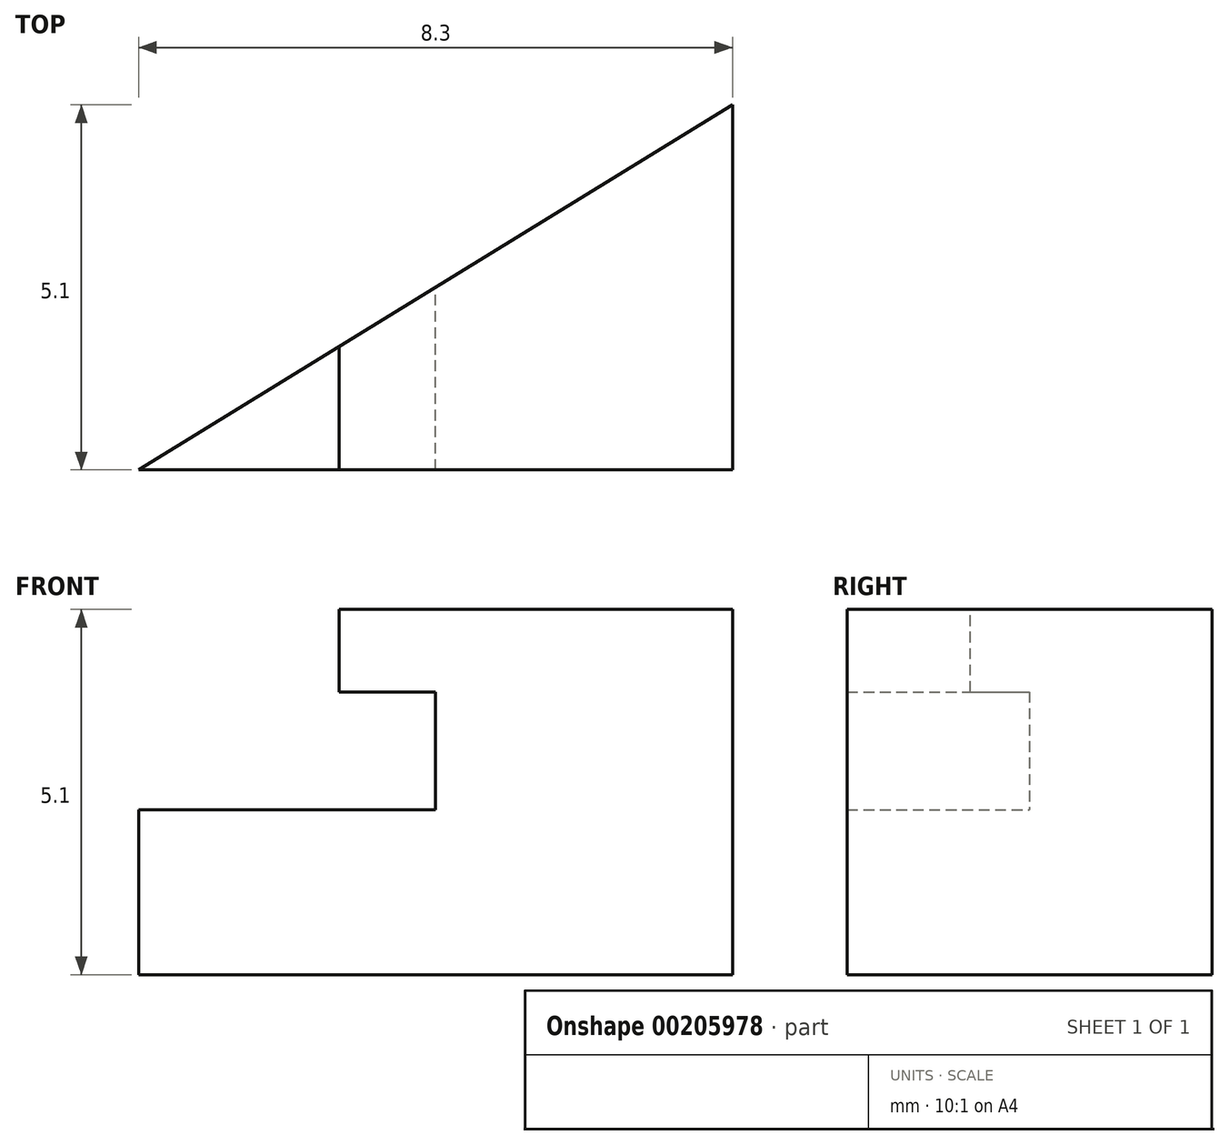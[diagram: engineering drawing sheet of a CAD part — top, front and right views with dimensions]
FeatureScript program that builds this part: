
annotation { "Feature Type Name" : "Feature", "Feature Type Description" : "" }
export const myFeature = defineFeature(function(context is Context, id is Id, definition is map)
    precondition{}
    {
        {
            var Q0;
            Q0=qCreatedBy(makeId("Top.planeOp"),FACE);
            var sketch = newSketch(context, id + "F0", { "sketchPlane" : qUnion([Q0])});
            skLineSegment(sketch, "E0", {"start": v(0, 0) * mm, "end": v(-8.3, 0) * mm});
            skLineSegment(sketch, "E1", {"start": v(-8.3, 0) * mm, "end": v(0, 5.1) * mm});
            skLineSegment(sketch, "E2", {"start": v(0, 5.1) * mm, "end": v(0, 0) * mm});
            skLineSegment(sketch, "E3", {"start": v(0, 0) * mm, "end": v(-4.15, 0) * mm});
            skLineSegment(sketch, "E4", {"start": v(-4.15, 0) * mm, "end": v(-4.15, 2.55) * mm});
            skLineSegment(sketch, "E5", {"start": v(0, 0) * mm, "end": v(-5.5, 0) * mm});
            skLineSegment(sketch, "E6", {"start": v(-5.5, 0) * mm, "end": v(-5.5, 1.72) * mm});
            skSolve(sketch);
        }
        {
            var Q0;
            {var subQ0=sQuery(id+"F0.wireOp",EDGE,"E2");Q0=makeQuery(id+"F0.imprint","IMPRINT",FACE,{"disambiguationData":[TD([[makeQuery(id+"F0.imprint","IMPRINT",EDGE,{"derivedFrom":subQ0}),-1.0]])]});}
            var Q1;
            {var subQ0=sQuery(id+"F0.wireOp",EDGE,"E4");Q1=makeQuery(id+"F0.imprint","IMPRINT",FACE,{"disambiguationData":[TD([[makeQuery(id+"F0.imprint","IMPRINT",EDGE,{"derivedFrom":subQ0}),1.0]])]});}
            extrude(context, id + "F1", {"entities" : qUnion([Q0, Q1]), "oppositeDirection" : true, "depth" : 2.3 * mm, "hasSecondDirection" : true, "secondDirectionOppositeDirection" : false, "secondDirectionDepth" : 2.8 * mm});
        }
        {
            var Q0;
            {var subQ0=sQuery(id+"F0.wireOp",EDGE,"E0");Q0=makeQuery(id+"F0.imprint","IMPRINT",FACE,{"disambiguationData":[TD([[makeQuery(id+"F0.imprint","IMPRINT",EDGE,{"derivedFrom":subQ0}),-1.0]])]});}
            extrude(context, id + "F2", {"entities" : qUnion([Q0]), "operationType" : NewBodyOperationType.ADD, "oppositeDirection" : true, "depth" : 2.3 * mm});
        }
        {
            var Q0;
            {var subQ0=sQuery(id+"F0.wireOp",EDGE,"E4");Q0=makeQuery(id+"F0.imprint","IMPRINT",FACE,{"disambiguationData":[TD([[makeQuery(id+"F0.imprint","IMPRINT",EDGE,{"derivedFrom":subQ0}),1.0]])]});}
            extrude(context, id + "F3", {"entities" : qUnion([Q0]), "operationType" : NewBodyOperationType.REMOVE, "depth" : 1.65 * mm});
        }
    });
